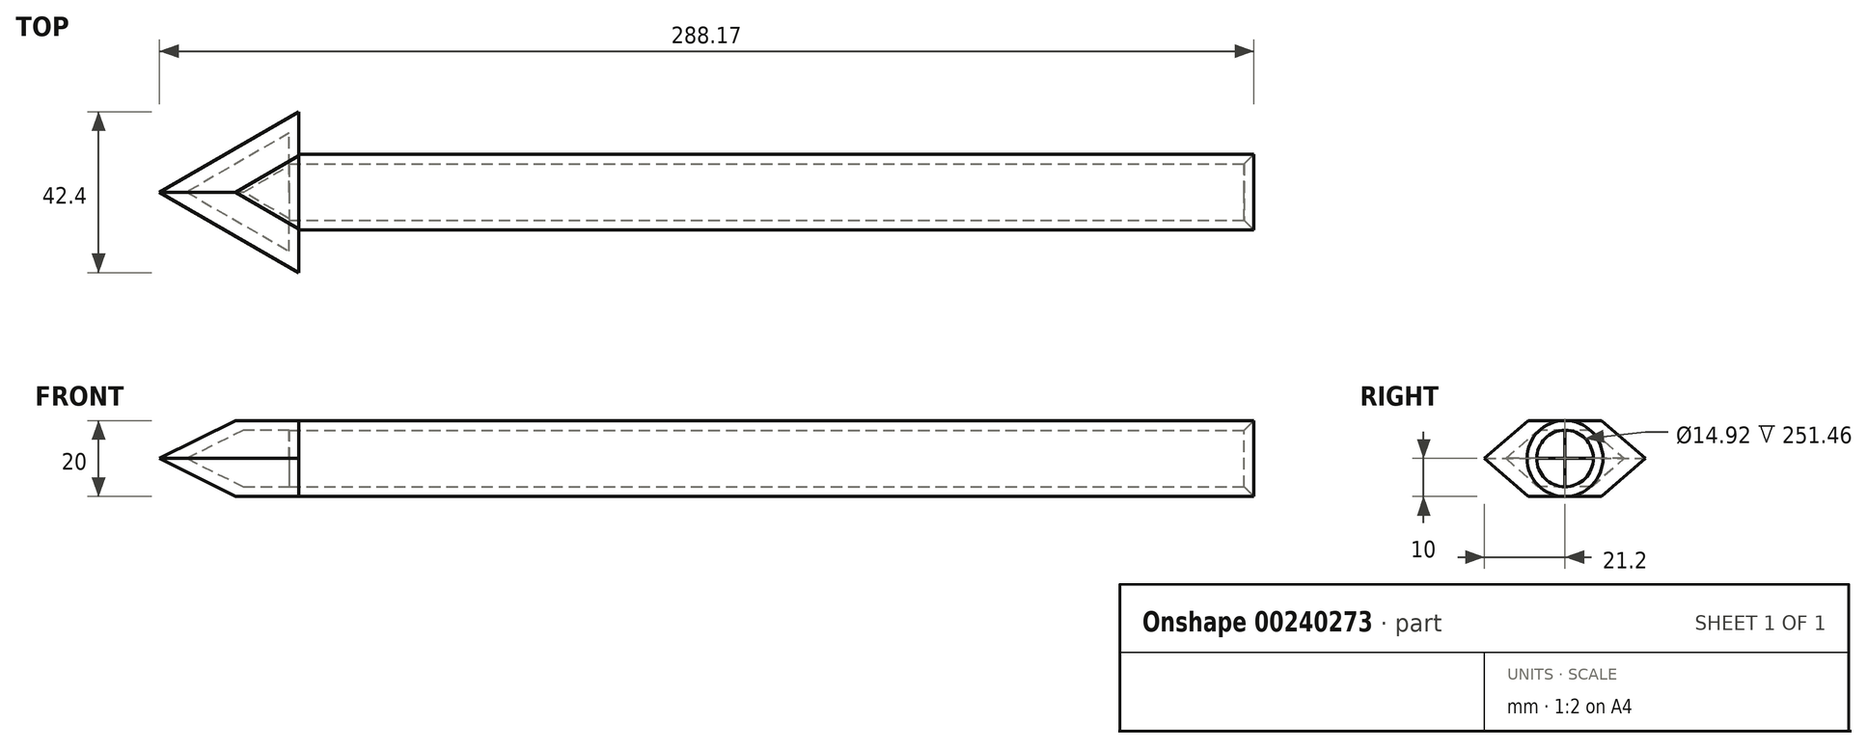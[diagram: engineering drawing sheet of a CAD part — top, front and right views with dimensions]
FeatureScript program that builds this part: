
annotation { "Feature Type Name" : "Feature", "Feature Type Description" : "" }
export const myFeature = defineFeature(function(context is Context, id is Id, definition is map)
    precondition{}
    {
        {
            var Q0;
            Q0=qCreatedBy(makeId("Top.planeOp"),FACE);
            var sketch = newSketch(context, id + "F0", { "sketchPlane" : qUnion([Q0])});
            skLineSegment(sketch, "E0.bottom", {"start": v(-127, 10) * mm, "end": v(127, 10) * mm});
            skLineSegment(sketch, "E0.top", {"start": v(-127, -10) * mm, "end": v(127, -10) * mm});
            skLineSegment(sketch, "E0.left", {"start": v(-127, 10) * mm, "end": v(-127, -10) * mm});
            skLineSegment(sketch, "E0.right", {"start": v(127, 10) * mm, "end": v(127, -10) * mm});
            skPoint(sketch, "E0.middle", {"position": v(0, 0) * mm});
            skCircle(sketch, "E1.cCircle", {"center": v(-139.24, 0) * mm, "radius": 12.24 * mm, "construction": true});
            skLineSegment(sketch, "E1.0", {"start": v(-127, 21.2) * mm, "end": v(-127, -21.2) * mm});
            skLineSegment(sketch, "E1.1", {"start": v(-127, -21.2) * mm, "end": v(-163.71, 0) * mm});
            skLineSegment(sketch, "E1.2", {"start": v(-163.71, 0) * mm, "end": v(-127, 21.2) * mm});
            skPoint(sketch, "E1.0.midPoint", {"position": v(-127, 0) * mm});
            skSolve(sketch);
        }
        {
            var Q0;
            {var subQ0=sQuery(id+"F0.wireOp",EDGE,"E1.1");Q0=makeQuery(id+"F0.imprint","IMPRINT",FACE,{"disambiguationData":[TD([[makeQuery(id+"F0.imprint","IMPRINT",EDGE,{"derivedFrom":subQ0}),-1.0]])]});}
            var Q1;
            {var subQ0=sQuery(id+"F0.wireOp",EDGE,"E0.bottom");Q1=makeQuery(id+"F0.imprint","IMPRINT",FACE,{"disambiguationData":[TD([[makeQuery(id+"F0.imprint","IMPRINT",EDGE,{"derivedFrom":subQ0}),-1.0]])]});}
            extrude(context, id + "F1", {"entities" : qUnion([Q0, Q1]), "endBound" : BoundingType.SYMMETRIC, "depth" : 20 * mm});
        }
        {
            var Q0;
            Q0=makeQuery(id+"F1.opExtrude","CAP_EDGE",EDGE,{"disambiguationData":[OSD([sQuery(id+"F0.wireOp",EDGE,"E0.top")])],"isStart":false});
            var Q1;
            Q1=makeQuery(id+"F1.opExtrude","CAP_EDGE",EDGE,{"disambiguationData":[OSD([sQuery(id+"F0.wireOp",EDGE,"E0.bottom")])],"isStart":false});
            var Q2;
            Q2=makeQuery(id+"F1.opExtrude","CAP_EDGE",EDGE,{"disambiguationData":[OSD([sQuery(id+"F0.wireOp",EDGE,"E0.bottom")])],"isStart":true});
            var Q3;
            Q3=makeQuery(id+"F1.opExtrude","CAP_EDGE",EDGE,{"disambiguationData":[OSD([sQuery(id+"F0.wireOp",EDGE,"E0.top")])],"isStart":true});
            fillet(context, id + "F2", {"entities" : qUnion([Q0, Q1, Q2, Q3]), "radius" : 10 * mm, "tangentPropagation" : true, "allowEdgeOverflow" : false});
        }
        {
            var Q0;
            Q0=makeQuery(id+"F1.opExtrude","CAP_EDGE",EDGE,{"disambiguationData":[OSD([sQuery(id+"F0.wireOp",EDGE,"E1.2")])],"isStart":false});
            var Q1;
            Q1=makeQuery(id+"F1.opExtrude","CAP_EDGE",EDGE,{"disambiguationData":[OSD([sQuery(id+"F0.wireOp",EDGE,"E1.1")])],"isStart":false});
            var Q2;
            Q2=makeQuery(id+"F1.opExtrude","CAP_EDGE",EDGE,{"disambiguationData":[OSD([sQuery(id+"F0.wireOp",EDGE,"E1.1")])],"isStart":true});
            var Q3;
            Q3=makeQuery(id+"F1.opExtrude","CAP_EDGE",EDGE,{"disambiguationData":[OSD([sQuery(id+"F0.wireOp",EDGE,"E1.2")])],"isStart":true});
            chamfer(context, id + "F3", {"entities" : qUnion([Q0, Q1, Q2, Q3]), "width" : 10 * mm, "tangentPropagation" : true});
        }
        {
            var Q0;
            Q0=makeQuery(id+"F1.opExtrude","SWEPT_FACE",FACE,{"disambiguationData":[OSD([sQuery(id+"F0.wireOp",EDGE,"E0.right")])]});
            shell(context, id + "F4", {"entities" : qUnion([Q0]), "thickness" : 2.54 * mm});
        }
        {
            var Q0;
            Q0=makeQuery(id+"F4.opShell","OFFSET_EDGE",EDGE,{"disambiguationData":[OSD([sQuery(id+"F0.wireOp",EDGE,"E0.bottom"),sQuery(id+"F0.wireOp",EDGE,"E0.right")])]});
            chamfer(context, id + "F5", {"entities" : qUnion([Q0]), "width" : 5.08 * mm, "tangentPropagation" : true});
        }
    });
